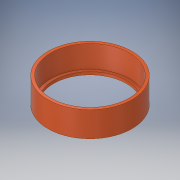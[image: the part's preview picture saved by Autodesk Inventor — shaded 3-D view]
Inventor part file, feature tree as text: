
AUTODESK INVENTOR PART (.ipt)
format: ipt  version: 2017 (Build 210142000, 142)  size: 119,296 bytes
history: native  units: in
note: dims shown in document units (in); Inventor stores cm internally (conversion verified against a paired STEP export)
features: extrude x2, sketch x2, projected_geometry x1
ambient origin geometry x8: Origin, YZ Plane, XZ Plane, XY Plane, X Axis, Y Axis, Z Axis, Center Point
bodies: Solid1 (feature_tree)
feature tree (5):
  extrude  "Extrusion1"  Depth=7.5in
  extrude  "Extrusion3"  Depth=0.25in
  sketch  "Sketch1"  dims[d0=7.0in d1=7.5in]
  sketch  "Sketch4"  dims[d2=2.25in d3=0.0in d8=6.5in d9=0.25in d10=0.0in]
  projected_geometry  "Projected Loop2"
